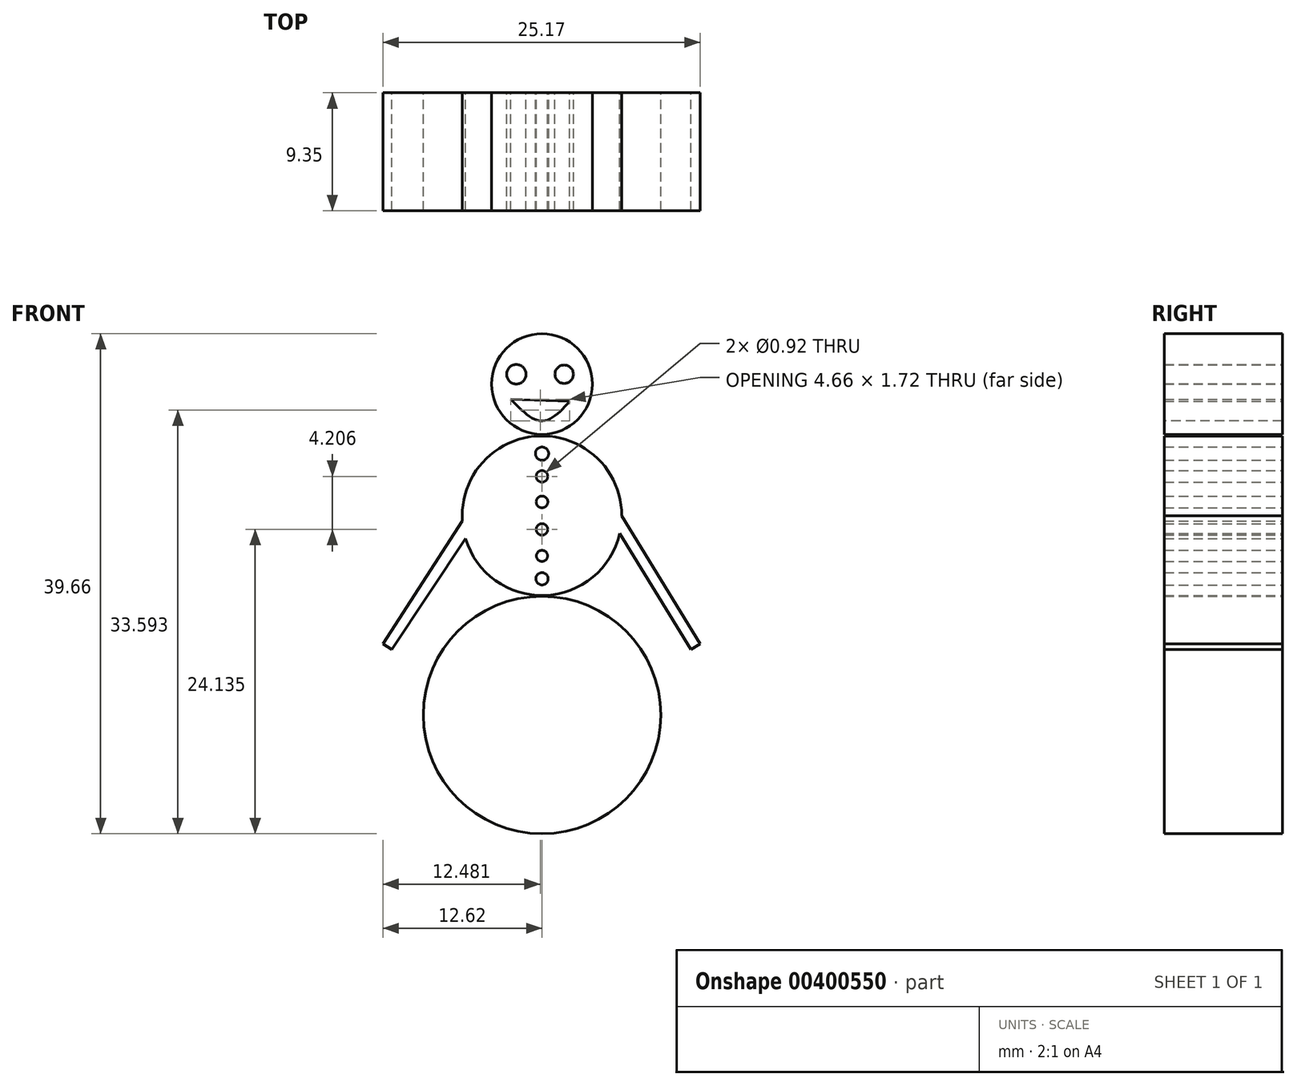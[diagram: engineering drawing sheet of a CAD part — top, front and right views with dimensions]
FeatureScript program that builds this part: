
annotation { "Feature Type Name" : "Feature", "Feature Type Description" : "" }
export const myFeature = defineFeature(function(context is Context, id is Id, definition is map)
    precondition{}
    {
        {
            var Q0;
            Q0=qCreatedBy(makeId("Front.planeOp"),FACE);
            var sketch = newSketch(context, id + "F0", { "sketchPlane" : qUnion([Q0])});
            skCircle(sketch, "E0", {"center": v(0, 55.97) * mm, "radius": 10.85 * mm});
            skCircle(sketch, "E1", {"center": v(0, 27.59) * mm, "radius": 17.19 * mm});
            skCircle(sketch, "E2", {"center": v(0, -15.37) * mm, "radius": 25.58 * mm});
            skLineSegment(sketch, "E3", {"start": v(-17.15, 26.4) * mm, "end": v(-34.3, 0) * mm});
            skLineSegment(sketch, "E4", {"start": v(17.19, 27.59) * mm, "end": v(34.1, 0) * mm});
            skCircle(sketch, "E5", {"center": v(0, 36.06) * mm, "radius": 1.25 * mm});
            skCircle(sketch, "E6", {"center": v(0, 30.55) * mm, "radius": 1.26 * mm});
            skCircle(sketch, "E7", {"center": v(0, 24.63) * mm, "radius": 1.25 * mm});
            skCircle(sketch, "E8", {"center": v(0, 18.92) * mm, "radius": 1.2 * mm});
            skCircle(sketch, "E9", {"center": v(0, 14) * mm, "radius": 1.32 * mm});
            skCircle(sketch, "E10", {"center": v(-5.53, 58.07) * mm, "radius": 2.1 * mm});
            skCircle(sketch, "E11", {"center": v(4.78, 58.07) * mm, "radius": 1.99 * mm});
            skCircle(sketch, "E12", {"center": v(0, 40.96) * mm, "radius": 1.43 * mm});
            skCircle(sketch, "E13", {"center": v(107.43, 25.02) * mm, "radius": 1.2 * mm});
            skFitSpline(sketch, "E14", {"points": [v(-6.7, 52.68) * mm, v(0, 47.99) * mm, v(5.95, 52.2) * mm], "startDerivative": vector(13.24, -13.69) * mm, "endDerivative": vector(12.06, 13) * mm});
            skLineSegment(sketch, "E15", {"start": v(-6.7, 52.68) * mm, "end": v(5.95, 52.2) * mm});
            skLineSegment(sketch, "E16", {"start": v(-34.3, 0) * mm, "end": v(-32.38, -1.24) * mm});
            skLineSegment(sketch, "E17", {"start": v(-32.38, -1.24) * mm, "end": v(-16.46, 22.64) * mm});
            skLineSegment(sketch, "E18", {"start": v(34.1, 0) * mm, "end": v(32.07, -1.24) * mm});
            skLineSegment(sketch, "E19", {"start": v(32.07, -1.24) * mm, "end": v(16.75, 23.75) * mm});
            skSolve(sketch);
        }
        {
            var Q0;
            Q0=makeQuery(id+"F0.imprint","IMPRINT",FACE,{"disambiguationData":[TD([[makeQuery(id+"F0.imprint","IMPRINT",EDGE,{"derivedFrom":sQuery(id+"F0.wireOp",EDGE,"E0")}),1.0]])]});
            var Q1;
            Q1=makeQuery(id+"F0.imprint","IMPRINT",FACE,{"disambiguationData":[TD([[makeQuery(id+"F0.imprint","IMPRINT",EDGE,{"derivedFrom":sQuery(id+"F0.wireOp",EDGE,"E5")}),-1.0]])]});
            var Q2;
            Q2=makeQuery(id+"F0.imprint","IMPRINT",FACE,{"disambiguationData":[TD([[makeQuery(id+"F0.imprint","IMPRINT",EDGE,{"derivedFrom":sQuery(id+"F0.wireOp",EDGE,"E2")}),1.0]])]});
            var Q3;
            {var subQ0=sQuery(id+"F0.wireOp",EDGE,"E3");Q3=makeQuery(id+"F0.imprint","IMPRINT",FACE,{"disambiguationData":[TD([[makeQuery(id+"F0.imprint","IMPRINT",EDGE,{"derivedFrom":subQ0}),1.0]])]});}
            var Q4;
            {var subQ0=sQuery(id+"F0.wireOp",EDGE,"E4");Q4=makeQuery(id+"F0.imprint","IMPRINT",FACE,{"disambiguationData":[TD([[makeQuery(id+"F0.imprint","IMPRINT",EDGE,{"derivedFrom":subQ0}),-1.0]])]});}
            extrude(context, id + "F1", {"entities" : qUnion([Q0, Q1, Q2, Q3, Q4]), "depth" : 25.4 * mm});
        }
        {
            var Q0;
            Q0=makeQuery(id+"F1.opExtrude","SWEPT_BODY",BODY,{"disambiguationData":[OSD([sQuery(id+"F0.wireOp",EDGE,"E1"),sQuery(id+"F0.wireOp",EDGE,"E3"),sQuery(id+"F0.wireOp",EDGE,"E4"),sQuery(id+"F0.wireOp",EDGE,"E5"),sQuery(id+"F0.wireOp",EDGE,"E6"),sQuery(id+"F0.wireOp",EDGE,"E7"),sQuery(id+"F0.wireOp",EDGE,"E8"),sQuery(id+"F0.wireOp",EDGE,"E9"),sQuery(id+"F0.wireOp",EDGE,"E12"),sQuery(id+"F0.wireOp",EDGE,"E16"),sQuery(id+"F0.wireOp",EDGE,"E17"),sQuery(id+"F0.wireOp",EDGE,"E18"),sQuery(id+"F0.wireOp",EDGE,"E19")])]});
            var Q1;
            Q1=makeQuery(id+"F1.opExtrude","SWEPT_BODY",BODY,{"disambiguationData":[OSD([sQuery(id+"F0.wireOp",EDGE,"E2")])]});
            var Q2;
            Q2=makeQuery(id+"F1.opExtrude","SWEPT_BODY",BODY,{"disambiguationData":[OSD([sQuery(id+"F0.wireOp",EDGE,"E0"),sQuery(id+"F0.wireOp",EDGE,"E10"),sQuery(id+"F0.wireOp",EDGE,"E11"),sQuery(id+"F0.wireOp",EDGE,"E14"),sQuery(id+"F0.wireOp",EDGE,"E15")])]});
            var Q3;
            Q3=qCreatedBy(makeId("Origin.pointOp"),VERTEX);
            transform(context, id + "F2", {"entities" : qUnion([Q0, Q1, Q2]), "transformType" : TransformType.SCALE_UNIFORMLY, "scale" : 0.46, "scalePoint" : qUnion([Q3]), "makeCopy" : false});
        }
        {
            var Q0;
            Q0=makeQuery(id+"F1.opExtrude","SWEPT_BODY",BODY,{"disambiguationData":[OSD([sQuery(id+"F0.wireOp",EDGE,"E1"),sQuery(id+"F0.wireOp",EDGE,"E3"),sQuery(id+"F0.wireOp",EDGE,"E4"),sQuery(id+"F0.wireOp",EDGE,"E5"),sQuery(id+"F0.wireOp",EDGE,"E6"),sQuery(id+"F0.wireOp",EDGE,"E7"),sQuery(id+"F0.wireOp",EDGE,"E8"),sQuery(id+"F0.wireOp",EDGE,"E9"),sQuery(id+"F0.wireOp",EDGE,"E12"),sQuery(id+"F0.wireOp",EDGE,"E16"),sQuery(id+"F0.wireOp",EDGE,"E17"),sQuery(id+"F0.wireOp",EDGE,"E18"),sQuery(id+"F0.wireOp",EDGE,"E19")])]});
            var Q1;
            Q1=makeQuery(id+"F1.opExtrude","SWEPT_BODY",BODY,{"disambiguationData":[OSD([sQuery(id+"F0.wireOp",EDGE,"E2")])]});
            var Q2;
            Q2=makeQuery(id+"F1.opExtrude","SWEPT_BODY",BODY,{"disambiguationData":[OSD([sQuery(id+"F0.wireOp",EDGE,"E0"),sQuery(id+"F0.wireOp",EDGE,"E10"),sQuery(id+"F0.wireOp",EDGE,"E11"),sQuery(id+"F0.wireOp",EDGE,"E14"),sQuery(id+"F0.wireOp",EDGE,"E15")])]});
            var Q3;
            Q3=qCreatedBy(makeId("Origin.pointOp"),VERTEX);
            var Q4;
            Q4=qCreatedBy(makeId("Origin.pointOp"),VERTEX);
            transform(context, id + "F3", {"entities" : qUnion([Q0, Q1, Q2]), "transformType" : TransformType.SCALE_UNIFORMLY, "scale" : .5, "scalePoint" : qUnion([Q4]), "makeCopy" : false});
        }
        {
            var Q0;
            Q0=makeQuery(id+"F1.opExtrude","SWEPT_BODY",BODY,{"disambiguationData":[OSD([sQuery(id+"F0.wireOp",EDGE,"E1"),sQuery(id+"F0.wireOp",EDGE,"E3"),sQuery(id+"F0.wireOp",EDGE,"E4"),sQuery(id+"F0.wireOp",EDGE,"E5"),sQuery(id+"F0.wireOp",EDGE,"E6"),sQuery(id+"F0.wireOp",EDGE,"E7"),sQuery(id+"F0.wireOp",EDGE,"E8"),sQuery(id+"F0.wireOp",EDGE,"E9"),sQuery(id+"F0.wireOp",EDGE,"E12"),sQuery(id+"F0.wireOp",EDGE,"E16"),sQuery(id+"F0.wireOp",EDGE,"E17"),sQuery(id+"F0.wireOp",EDGE,"E18"),sQuery(id+"F0.wireOp",EDGE,"E19")])]});
            var Q1;
            Q1=makeQuery(id+"F1.opExtrude","SWEPT_BODY",BODY,{"disambiguationData":[OSD([sQuery(id+"F0.wireOp",EDGE,"E2")])]});
            var Q2;
            Q2=makeQuery(id+"F1.opExtrude","SWEPT_BODY",BODY,{"disambiguationData":[OSD([sQuery(id+"F0.wireOp",EDGE,"E0"),sQuery(id+"F0.wireOp",EDGE,"E10"),sQuery(id+"F0.wireOp",EDGE,"E11"),sQuery(id+"F0.wireOp",EDGE,"E14"),sQuery(id+"F0.wireOp",EDGE,"E15")])]});
            var Q3;
            Q3=qCreatedBy(makeId("Origin.pointOp"),VERTEX);
            var Q4;
            Q4=qCreatedBy(makeId("Origin.pointOp"),VERTEX);
            transform(context, id + "F4", {"entities" : qUnion([Q0, Q1, Q2]), "transformType" : TransformType.SCALE_UNIFORMLY, "scale" : 1.6, "scalePoint" : qUnion([Q4]), "makeCopy" : false});
        }
    });
